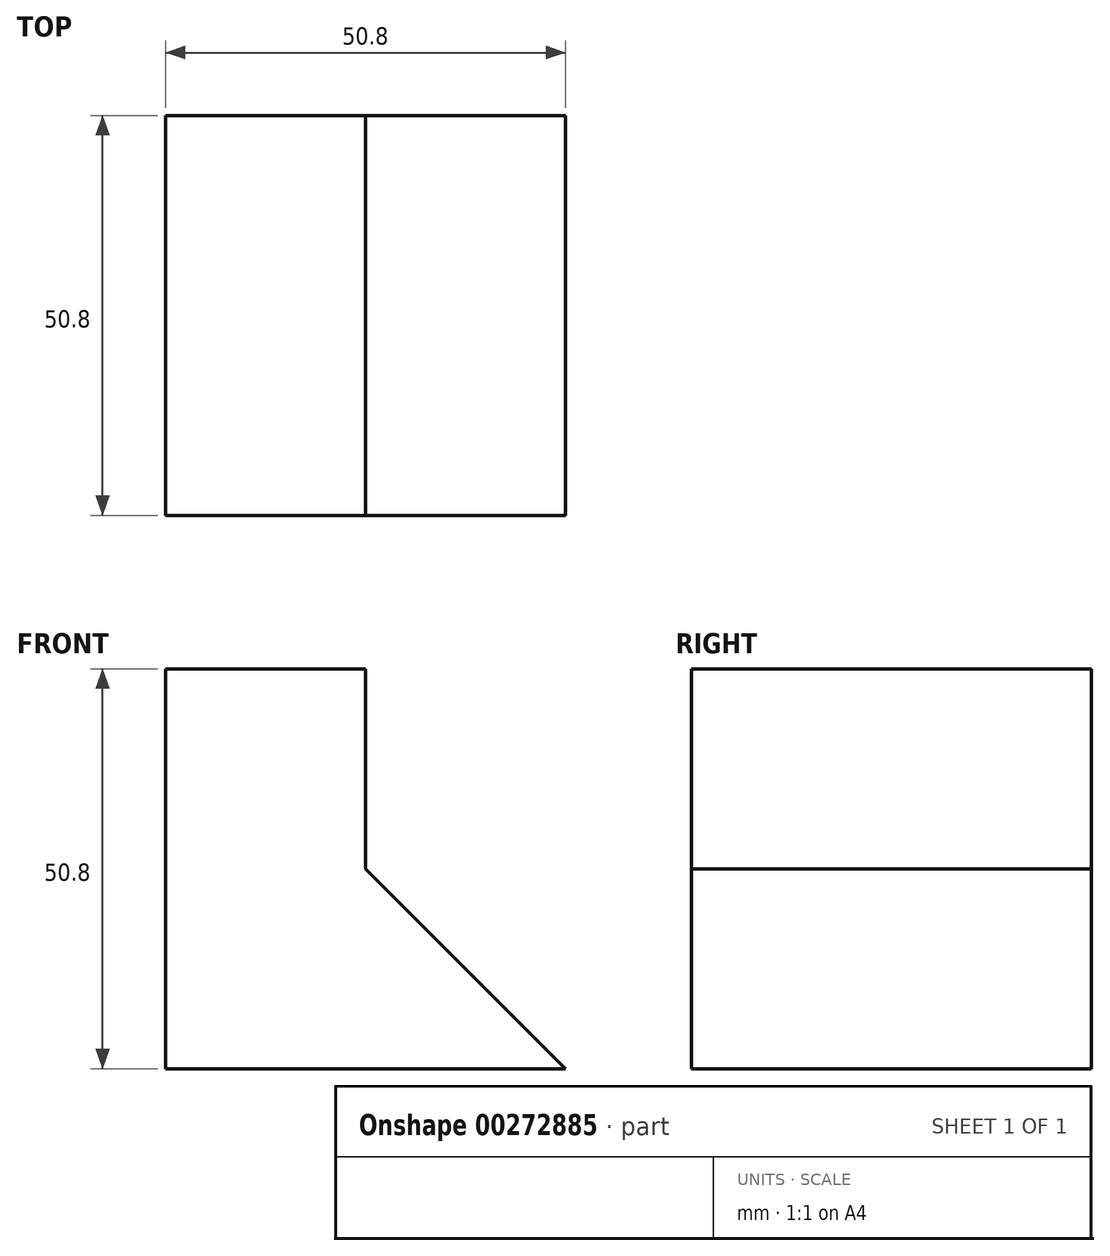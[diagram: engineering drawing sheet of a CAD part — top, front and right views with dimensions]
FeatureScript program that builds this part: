
annotation { "Feature Type Name" : "Feature", "Feature Type Description" : "" }
export const myFeature = defineFeature(function(context is Context, id is Id, definition is map)
    precondition{}
    {
        {
            var Q0;
            Q0=qCreatedBy(makeId("Front.planeOp"),FACE);
            var sketch = newSketch(context, id + "F0", { "sketchPlane" : qUnion([Q0])});
            skLineSegment(sketch, "E0", {"start": v(0, 0) * mm, "end": v(-50.8, 0) * mm});
            skLineSegment(sketch, "E1", {"start": v(-50.8, 0) * mm, "end": v(-50.8, 50.8) * mm});
            skLineSegment(sketch, "E2", {"start": v(-50.8, 50.8) * mm, "end": v(-25.4, 50.8) * mm});
            skLineSegment(sketch, "E3", {"start": v(-25.4, 50.8) * mm, "end": v(-25.4, 38.1) * mm});
            skLineSegment(sketch, "E4", {"start": v(-25.4, 38.1) * mm, "end": v(-25.4, 25.4) * mm});
            skLineSegment(sketch, "E5", {"start": v(-25.4, 25.4) * mm, "end": v(0, 0) * mm});
            skSolve(sketch);
        }
        {
            var Q0;
            Q0=makeQuery(id+"F0.imprint","IMPRINT",FACE,{"disambiguationData":[TD([[makeQuery(id+"F0.imprint","IMPRINT",EDGE,{"derivedFrom":sQuery(id+"F0.wireOp",EDGE,"E0")}),-1.0]])]});
            extrude(context, id + "F1", {"entities" : qUnion([Q0]), "depth" : 50.8 * mm});
        }
    });
